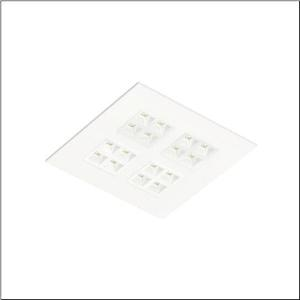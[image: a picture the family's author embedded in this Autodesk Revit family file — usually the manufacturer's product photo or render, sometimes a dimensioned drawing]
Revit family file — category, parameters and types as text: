
# Revit family: silica_31_square_51my6ndu34wa
name_source: partatom
category: Lighting Fixtures
units: mm (PartAtom-declared; Revit-internal decimal feet)

## family parameters
Cut with Voids When Loaded = No
Host = Face
Light Source = No
Part Type = Normal
Room Calculation Point = No
Round Connector Dimension = Use Diameter
Shared = No

## types (1)
- --- (1 x LED, 6230 lm, 38.5 W, 3000K)
    Apparent Load = 39 VA
    CIE Flux Codes = 81 99 100 100 100
    Color Rendering = 80
    Color Temperature = 3000K
    Default Elevation = 1800 mm
    Description = Silica 31 Square, office luminaire, primary light control with lens, of PMMA, primary anti-glare with reflector, of PC, white, light emission: direct distribution, primary light characteristic: symmetric, installation type: lay-in mounting, LED, rated luminous flux: 4.540lm, luminous efficacy: 162lm/W, light colour: 830, colour temperature: 3000K, control gear: DALI 2, Multilumen, with terminal, 5-pole, mains connection: 220..240V, AC, 50/60Hz, rated input power: 28W, luminaire housing, of sheet steel, coated, traffic white (RAL 9016), module: M625, length: 620mm, width: 620mm, height: 43mm, protection rating (complete): IP20, insulation class (complete): insulation class II (safety insulation), certification: CE, impact resistance: IK03, permissible operating ambient temperature: -20..+35°C, standard: EN 50419, packaging unit: 1 piece
    Height = 0 mm  [stored 0 ft]
    Lamp = 1 x LED
    Lamp Light Flux = 6230 lm
    Lamp Power = 38.5 W
    Lamp count = 1
    Length = 620 mm
    Luminous efficacy = 162 lm/W
    Manufacturer = Siteco
    ModVariant = No
    Model = 51MY6NDU34WA
    Mounting Place = Ceiling
    Mounting Type = Recessed
    Number of Poles = 1
    OnlyDefault = Yes
    Power Factor = 1
    Product Name = Silica 31 Square
    Product group = office luminaire | ceiling recessed
    ProductGroupID = 400
    Protection Class = Protection class II
    Protection Degree = IP 20
    RLX_Detail_Level = 1
    RLX_Emergency_Light_Flux = 0 lm
    RLX_Emergency_Type = 0
    RLX_Emergency_Type_DB = No
    RlxData = <blob elided: 28053 chars, md5=b4baa064>
    Socket = socket
    Standby Power = 0 W
    System Light Flux = 6230 lm
    System Power = 39 W
    Type Comments = factory setting: luminous flux: 100 % | (OFF | OFF | OFF | OFF) | 1050 mA
    Type Image = l_1313651.jpg
    URL = http://relux.com
    VarID = @adj_044653
    Voltage = 0 V
    Weight = 0.00 kg
    Width = 620 mm

note: [stored X ft] marks values corroborated as IEEE doubles in the binary element streams (Revit-internal decimal feet)

## geometry (parser evidence)
native form markers: Blend x4, Sweep x10
no freeform markers — native parametric forms only
